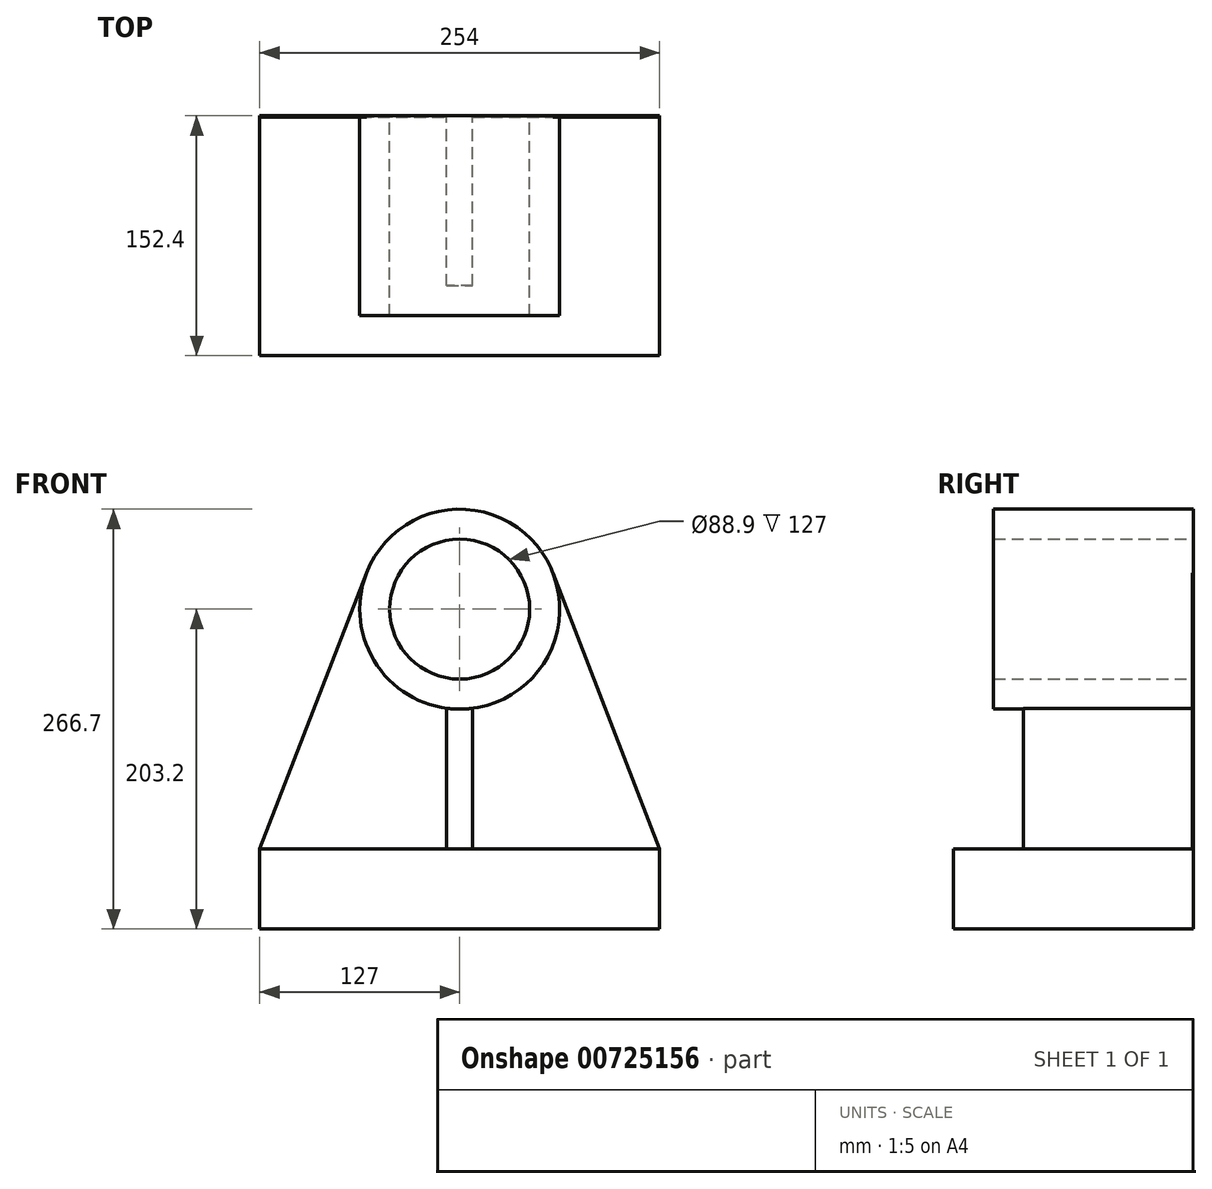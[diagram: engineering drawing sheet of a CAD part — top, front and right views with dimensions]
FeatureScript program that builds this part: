
annotation { "Feature Type Name" : "Feature", "Feature Type Description" : "" }
export const myFeature = defineFeature(function(context is Context, id is Id, definition is map)
    precondition{}
    {
        {
            assignVariable(context, id + "F0", {"name" : "C", "anyValue" : .75});
        }
        {
            var Q0;
            Q0=qCreatedBy(makeId("Front.planeOp"),FACE);
            var sketch = newSketch(context, id + "F1", { "sketchPlane" : qUnion([Q0])});
            skLineSegment(sketch, "E0", {"start": v(0, 0) * mm, "end": v(254, 0) * mm});
            skLineSegment(sketch, "E1", {"start": v(254, 0) * mm, "end": v(254, 50.8) * mm});
            skLineSegment(sketch, "E2", {"start": v(254, 50.8) * mm, "end": v(0, 50.8) * mm});
            skLineSegment(sketch, "E3", {"start": v(0, 50.8) * mm, "end": v(0, 0) * mm});
            skCircle(sketch, "E4", {"center": v(127, 203.2) * mm, "radius": 63.5 * mm});
            skPoint(sketch, "E4.centerSnap0", {"position": v(127, 50.8) * mm});
            skLineSegment(sketch, "E5", {"start": v(67.77, 226.1) * mm, "end": v(0, 50.8) * mm});
            skLineSegment(sketch, "E6", {"start": v(186.23, 226.1) * mm, "end": v(254, 50.8) * mm});
            skCircle(sketch, "E7", {"center": v(127, 203.2) * mm, "radius": 44.45 * mm});
            skLineSegment(sketch, "E8", {"start": v(118.75, 50.8) * mm, "end": v(118.75, 140.24) * mm});
            skLineSegment(sketch, "E9", {"start": v(135.26, 50.8) * mm, "end": v(135.26, 140.24) * mm});
            skSolve(sketch);
        }
        {
            var Q0;
            {var subQ0=sQuery(id+"F1.wireOp",EDGE,"E8");Q0=makeQuery(id+"F1.imprint","IMPRINT",FACE,{"disambiguationData":[TD([[makeQuery(id+"F1.imprint","IMPRINT",EDGE,{"derivedFrom":subQ0}),-1.0]])]});}
            extrude(context, id + "F2", {"entities" : qUnion([Q0]), "depth" : 107.95 * mm, "offsetDistance" : 25.4 * mm});
        }
        {
            var Q0;
            {var subQ0=sQuery(id+"F1.wireOp",EDGE,"E6");Q0=makeQuery(id+"F1.imprint","IMPRINT",FACE,{"disambiguationData":[TD([[makeQuery(id+"F1.imprint","IMPRINT",EDGE,{"derivedFrom":subQ0}),-1.0]])]});}
            extrude(context, id + "F3", {"entities" : qUnion([Q0]), "operationType" : NewBodyOperationType.ADD, "depth" : (getVariable(context, 'C')) * mm, "offsetDistance" : 25.4 * mm});
        }
        {
            var Q0;
            {var subQ0=sQuery(id+"F1.wireOp",EDGE,"E5");Q0=makeQuery(id+"F1.imprint","IMPRINT",FACE,{"disambiguationData":[TD([[makeQuery(id+"F1.imprint","IMPRINT",EDGE,{"derivedFrom":subQ0}),1.0]])]});}
            extrude(context, id + "F4", {"entities" : qUnion([Q0]), "operationType" : NewBodyOperationType.ADD, "depth" : (getVariable(context, 'C')) * mm, "offsetDistance" : 25.4 * mm});
        }
        {
            var Q0;
            Q0=makeQuery(id+"F1.imprint","IMPRINT",FACE,{"disambiguationData":[TD([[makeQuery(id+"F1.imprint","IMPRINT",EDGE,{"derivedFrom":sQuery(id+"F1.wireOp",EDGE,"E7")}),-1.0]])]});
            extrude(context, id + "F5", {"entities" : qUnion([Q0]), "operationType" : NewBodyOperationType.ADD, "depth" : 127 * mm, "offsetDistance" : 25.4 * mm});
        }
        {
            var Q0;
            Q0=makeQuery(id+"F1.imprint","IMPRINT",FACE,{"disambiguationData":[TD([[makeQuery(id+"F1.imprint","IMPRINT",EDGE,{"derivedFrom":sQuery(id+"F1.wireOp",EDGE,"E0")}),1.0]])]});
            extrude(context, id + "F6", {"entities" : qUnion([Q0]), "operationType" : NewBodyOperationType.ADD, "depth" : 152.4 * mm, "offsetDistance" : 25.4 * mm});
        }
    });
